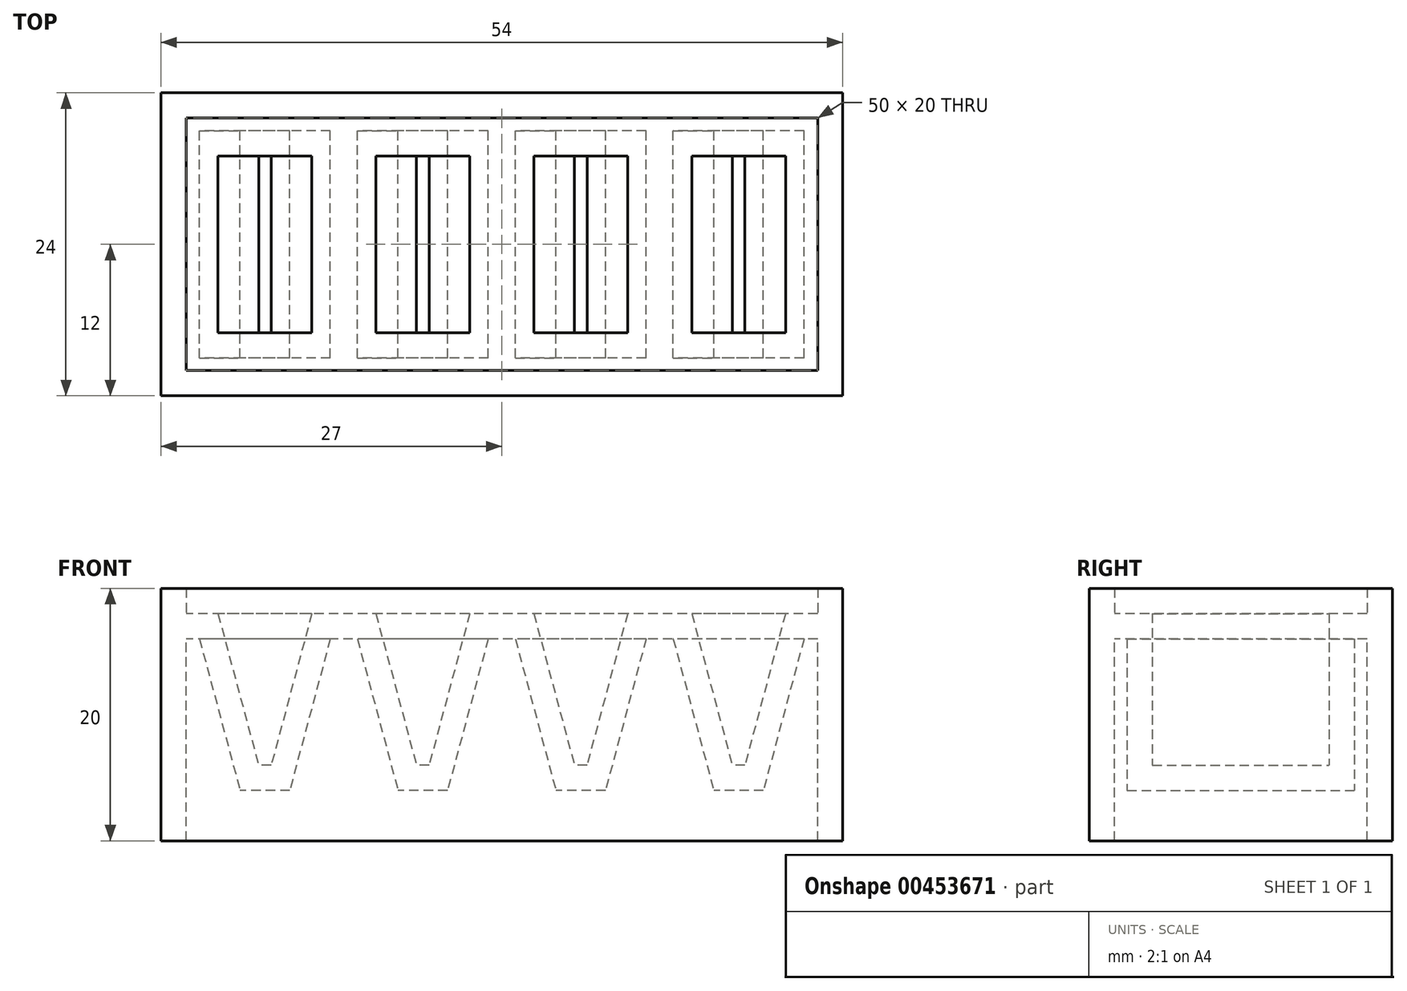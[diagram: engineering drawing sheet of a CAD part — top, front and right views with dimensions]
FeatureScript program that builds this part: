
annotation { "Feature Type Name" : "Feature", "Feature Type Description" : "" }
export const myFeature = defineFeature(function(context is Context, id is Id, definition is map)
    precondition{}
    {
        {
            var Q0;
            Q0=qCreatedBy(makeId("Right.planeOp"),FACE);
            var sketch = newSketch(context, id + "F0", { "sketchPlane" : qUnion([Q0])});
            skLineSegment(sketch, "E0", {"start": v(0, 0) * mm, "end": v(0, 18) * mm, "construction": true});
            skLineSegment(sketch, "E1", {"start": v(7, 18) * mm, "end": v(10, 18) * mm});
            skLineSegment(sketch, "E2", {"start": v(0, 0) * mm, "end": v(10, 0) * mm, "construction": true});
            skLineSegment(sketch, "E3", {"start": v(12, 0) * mm, "end": v(10, 0) * mm});
            skLineSegment(sketch, "E4", {"start": v(10, 0) * mm, "end": v(10, 16) * mm});
            skLineSegment(sketch, "E5", {"start": v(10, 16) * mm, "end": v(9, 16) * mm});
            skLineSegment(sketch, "E6", {"start": v(9, 16) * mm, "end": v(9, 4) * mm});
            skLineSegment(sketch, "E7", {"start": v(0, 4) * mm, "end": v(9, 4) * mm});
            skLineSegment(sketch, "E8", {"start": v(0, 6) * mm, "end": v(7, 6) * mm});
            skLineSegment(sketch, "E9", {"start": v(7, 18) * mm, "end": v(7, 6) * mm});
            skLineSegment(sketch, "E10.MirrorCS", {"start": v(0, 6) * mm, "end": v(-7, 6) * mm});
            skLineSegment(sketch, "E11.MirrorCS", {"start": v(0, 0) * mm, "end": v(-10, 0) * mm, "construction": true});
            skLineSegment(sketch, "E12.MirrorCS", {"start": v(0, 4) * mm, "end": v(-9, 4) * mm});
            skLineSegment(sketch, "E13.MirrorCS", {"start": v(-7, 18) * mm, "end": v(-7, 6) * mm});
            skLineSegment(sketch, "E14.MirrorCS", {"start": v(-12, 0) * mm, "end": v(-10, 0) * mm});
            skLineSegment(sketch, "E15.MirrorCS", {"start": v(-10, 0) * mm, "end": v(-10, 16) * mm});
            skLineSegment(sketch, "E16.MirrorCS", {"start": v(-10, 16) * mm, "end": v(-9, 16) * mm});
            skLineSegment(sketch, "E17.MirrorCS", {"start": v(-9, 16) * mm, "end": v(-9, 4) * mm});
            skLineSegment(sketch, "E18.bottom", {"start": v(10, 20) * mm, "end": v(12, 20) * mm});
            skLineSegment(sketch, "E18.left", {"start": v(10, 20) * mm, "end": v(10, 18) * mm});
            skLineSegment(sketch, "E19", {"start": v(10, 18) * mm, "end": v(10, 16) * mm, "construction": true});
            skLineSegment(sketch, "E20", {"start": v(12, 0) * mm, "end": v(12, 20) * mm});
            skLineSegment(sketch, "E21.MirrorCS", {"start": v(-7, 18) * mm, "end": v(-10, 18) * mm});
            skLineSegment(sketch, "E22.MirrorCS", {"start": v(-10, 20) * mm, "end": v(-10, 18) * mm});
            skLineSegment(sketch, "E23.MirrorCS", {"start": v(-10, 20) * mm, "end": v(-12, 20) * mm});
            skLineSegment(sketch, "E24.MirrorCS", {"start": v(-12, 0) * mm, "end": v(-12, 20) * mm});
            skSolve(sketch);
        }
        {
            var Q0;
            Q0=makeQuery(id+"F0.imprint","IMPRINT",FACE,{"disambiguationData":[TD([[makeQuery(id+"F0.imprint","IMPRINT",EDGE,{"derivedFrom":sQuery(id+"F0.wireOp",EDGE,"E1")}),-1.0]])]});
            extrude(context, id + "F1", {"entities" : qUnion([Q0]), "depth" : 50 * mm});
        }
        {
            var Q0;
            Q0=qCreatedBy(makeId("Front.planeOp"),FACE);
            var sketch = newSketch(context, id + "F2", { "sketchPlane" : qUnion([Q0])});
            skLineSegment(sketch, "E25.bottom", {"start": v(37.5, 20) * mm, "end": v(39.5, 20) * mm, "construction": true});
            skLineSegment(sketch, "E26", {"start": v(38.57, 16) * mm, "end": v(41.78, 4) * mm});
            skLineSegment(sketch, "E27", {"start": v(41.78, 4) * mm, "end": v(45.71, 4) * mm});
            skLineSegment(sketch, "E28", {"start": v(48.93, 16) * mm, "end": v(45.71, 4) * mm});
            skLineSegment(sketch, "E29", {"start": v(40.03, 18) * mm, "end": v(43.25, 6) * mm});
            skLineSegment(sketch, "E30", {"start": v(50, 20) * mm, "end": v(48, 20) * mm, "construction": true});
            skLineSegment(sketch, "E31", {"start": v(47.46, 18) * mm, "end": v(44.25, 6) * mm});
            skLineSegment(sketch, "E32", {"start": v(44.25, 6) * mm, "end": v(43.25, 6) * mm});
            skLineSegment(sketch, "E33", {"start": v(38.03, 18) * mm, "end": v(40.03, 18) * mm});
            skLineSegment(sketch, "E34", {"start": v(39.5, 20) * mm, "end": v(40.03, 18) * mm, "construction": true});
            skLineSegment(sketch, "E35", {"start": v(38.03, 18) * mm, "end": v(37.5, 20) * mm, "construction": true});
            skLineSegment(sketch, "E36", {"start": v(47.46, 18) * mm, "end": v(49.46, 18) * mm});
            skLineSegment(sketch, "E37", {"start": v(48, 20) * mm, "end": v(47.46, 18) * mm, "construction": true});
            skLineSegment(sketch, "E38", {"start": v(50, 20) * mm, "end": v(49.46, 18) * mm, "construction": true});
            skLineSegment(sketch, "E39", {"start": v(50, 16) * mm, "end": v(50, 4) * mm});
            skLineSegment(sketch, "E40", {"start": v(50, 4) * mm, "end": v(45.71, 4) * mm});
            skLineSegment(sketch, "E41", {"start": v(50, 16) * mm, "end": v(48.93, 16) * mm});
            skLineSegment(sketch, "E42", {"start": v(50, 16) * mm, "end": v(50, 20) * mm, "construction": true});
            skLineSegment(sketch, "E43", {"start": v(49.46, 18) * mm, "end": v(50, 18) * mm});
            skLineSegment(sketch, "E44", {"start": v(50, 16) * mm, "end": v(50, 18) * mm});
            skLineSegment(sketch, "E45", {"start": v(48.93, 16) * mm, "end": v(49.46, 18) * mm, "construction": true});
            skLineSegment(sketch, "E46", {"start": v(37.5, 20) * mm, "end": v(37.5, 18) * mm, "construction": true});
            skLineSegment(sketch, "E47", {"start": v(38.57, 16) * mm, "end": v(37.5, 16) * mm});
            skLineSegment(sketch, "E48", {"start": v(38.03, 18) * mm, "end": v(37.5, 18) * mm});
            skLineSegment(sketch, "E49", {"start": v(38.57, 16) * mm, "end": v(38.03, 18) * mm, "construction": true});
            skLineSegment(sketch, "E50", {"start": v(37.5, 4) * mm, "end": v(41.78, 4) * mm});
            skLineSegment(sketch, "E51.MirrorCS", {"start": v(36.43, 16) * mm, "end": v(37.5, 16) * mm});
            skLineSegment(sketch, "E52.MirrorCS", {"start": v(36.43, 16) * mm, "end": v(33.21, 4) * mm});
            skLineSegment(sketch, "E53.MirrorCS", {"start": v(33.21, 4) * mm, "end": v(29.28, 4) * mm});
            skLineSegment(sketch, "E54.MirrorCS", {"start": v(26.07, 16) * mm, "end": v(29.28, 4) * mm});
            skLineSegment(sketch, "E55.MirrorCS", {"start": v(25, 16) * mm, "end": v(26.07, 16) * mm});
            skLineSegment(sketch, "E56.MirrorCS", {"start": v(36.96, 18) * mm, "end": v(34.96, 18) * mm});
            skLineSegment(sketch, "E57.MirrorCS", {"start": v(36.96, 18) * mm, "end": v(37.5, 18) * mm});
            skLineSegment(sketch, "E58.MirrorCS", {"start": v(34.96, 18) * mm, "end": v(31.75, 6) * mm});
            skLineSegment(sketch, "E59.MirrorCS", {"start": v(30.75, 6) * mm, "end": v(31.75, 6) * mm});
            skLineSegment(sketch, "E60.MirrorCS", {"start": v(27.53, 18) * mm, "end": v(30.75, 6) * mm});
            skLineSegment(sketch, "E61.MirrorCS", {"start": v(27.53, 18) * mm, "end": v(25.53, 18) * mm});
            skLineSegment(sketch, "E62.MirrorCS", {"start": v(25.53, 18) * mm, "end": v(25, 18) * mm});
            skLineSegment(sketch, "E63.MirrorCS", {"start": v(25, 16) * mm, "end": v(25, 18) * mm, "construction": true});
            skLineSegment(sketch, "E64.MirrorCS", {"start": v(25, 4) * mm, "end": v(29.28, 4) * mm});
            skLineSegment(sketch, "E65.MirrorCS", {"start": v(37.5, 4) * mm, "end": v(33.21, 4) * mm});
            skLineSegment(sketch, "E66.MirrorCS", {"start": v(24.46, 18) * mm, "end": v(25, 18) * mm});
            skLineSegment(sketch, "E67.MirrorCS", {"start": v(22.46, 18) * mm, "end": v(24.46, 18) * mm});
            skLineSegment(sketch, "E68.MirrorCS", {"start": v(22.46, 18) * mm, "end": v(19.24, 6) * mm});
            skLineSegment(sketch, "E69.MirrorCS", {"start": v(19.24, 6) * mm, "end": v(18.24, 6) * mm});
            skLineSegment(sketch, "E70.MirrorCS", {"start": v(15.03, 18) * mm, "end": v(18.24, 6) * mm});
            skLineSegment(sketch, "E71.MirrorCS", {"start": v(13.03, 18) * mm, "end": v(15.03, 18) * mm});
            skLineSegment(sketch, "E72.MirrorCS", {"start": v(13.03, 18) * mm, "end": v(12.5, 18) * mm});
            skLineSegment(sketch, "E73.MirrorCS", {"start": v(11.96, 18) * mm, "end": v(12.5, 18) * mm});
            skLineSegment(sketch, "E74.MirrorCS", {"start": v(11.96, 18) * mm, "end": v(9.96, 18) * mm});
            skLineSegment(sketch, "E75.MirrorCS", {"start": v(9.96, 18) * mm, "end": v(6.74, 6) * mm});
            skLineSegment(sketch, "E76.MirrorCS", {"start": v(5.74, 6) * mm, "end": v(6.74, 6) * mm});
            skLineSegment(sketch, "E77.MirrorCS", {"start": v(2.53, 18) * mm, "end": v(5.74, 6) * mm});
            skLineSegment(sketch, "E78.MirrorCS", {"start": v(2.53, 18) * mm, "end": v(0.53, 18) * mm});
            skLineSegment(sketch, "E79.MirrorCS", {"start": v(0.53, 18) * mm, "end": v(-0.01, 18) * mm});
            skLineSegment(sketch, "E80.MirrorCS", {"start": v(-0.01, 16) * mm, "end": v(-0.01, 18) * mm});
            skLineSegment(sketch, "E81.MirrorCS", {"start": v(-0.01, 16) * mm, "end": v(1.06, 16) * mm});
            skLineSegment(sketch, "E82.MirrorCS", {"start": v(1.06, 16) * mm, "end": v(4.28, 4) * mm});
            skLineSegment(sketch, "E83.MirrorCS", {"start": v(8.2, 4) * mm, "end": v(4.28, 4) * mm});
            skLineSegment(sketch, "E84.MirrorCS", {"start": v(11.42, 16) * mm, "end": v(8.2, 4) * mm});
            skLineSegment(sketch, "E85.MirrorCS", {"start": v(11.42, 16) * mm, "end": v(12.5, 16) * mm});
            skLineSegment(sketch, "E86.MirrorCS", {"start": v(13.56, 16) * mm, "end": v(12.5, 16) * mm});
            skLineSegment(sketch, "E87.MirrorCS", {"start": v(13.56, 16) * mm, "end": v(16.78, 4) * mm});
            skLineSegment(sketch, "E88.MirrorCS", {"start": v(16.78, 4) * mm, "end": v(20.7, 4) * mm});
            skLineSegment(sketch, "E89.MirrorCS", {"start": v(23.92, 16) * mm, "end": v(20.7, 4) * mm});
            skLineSegment(sketch, "E90.MirrorCS", {"start": v(25, 16) * mm, "end": v(23.92, 16) * mm});
            skLineSegment(sketch, "E91.MirrorCS", {"start": v(25, 4) * mm, "end": v(20.7, 4) * mm});
            skPoint(sketch, "E92.MirrorCS.end.orphan", {"position": v(25, 4) * mm});
            skPoint(sketch, "E92.MirrorCS.start.orphan", {"position": v(25, 16) * mm});
            skLineSegment(sketch, "E93.MirrorCS", {"start": v(12.5, 4) * mm, "end": v(16.78, 4) * mm});
            skLineSegment(sketch, "E94.MirrorCS", {"start": v(12.5, 4) * mm, "end": v(8.2, 4) * mm});
            skLineSegment(sketch, "E95.MirrorCS", {"start": v(-0.01, 4) * mm, "end": v(4.28, 4) * mm});
            skLineSegment(sketch, "E96.MirrorCS", {"start": v(-0.01, 16) * mm, "end": v(-0.01, 4) * mm});
            skSolve(sketch);
        }
        {
            var Q0;
            Q0=makeQuery(id+"F2.imprint","IMPRINT",FACE,{"disambiguationData":[TD([[makeQuery(id+"F2.imprint","IMPRINT",EDGE,{"derivedFrom":sQuery(id+"F2.wireOp",EDGE,"E26")}),1.0]])]});
            var Q1;
            Q1=makeQuery(id+"F2.imprint","IMPRINT",FACE,{"disambiguationData":[TD([[makeQuery(id+"F2.imprint","IMPRINT",EDGE,{"derivedFrom":sQuery(id+"F2.wireOp",EDGE,"Oqk51IUW-a7Uu-kslN-KpYw-qfUBox6aqXp0")}),-1.0]])]});
            extrude(context, id + "F3", {"entities" : qUnion([Q0, Q1]), "operationType" : NewBodyOperationType.ADD, "endBound" : BoundingType.SYMMETRIC, "depth" : 18 * mm});
        }
        {
            var Q0;
            Q0=makeQuery(id+"F2.imprint","IMPRINT",FACE,{"disambiguationData":[TD([[makeQuery(id+"F2.imprint","IMPRINT",EDGE,{"derivedFrom":sQuery(id+"F2.wireOp",EDGE,"E39")}),-1.0]])]});
            var Q1;
            Q1=makeQuery(id+"F2.imprint","IMPRINT",FACE,{"disambiguationData":[TD([[makeQuery(id+"F2.imprint","IMPRINT",EDGE,{"derivedFrom":sQuery(id+"F2.wireOp",EDGE,"E26")}),-1.0]])]});
            var Q2;
            Q2=makeQuery(id+"F2.imprint","IMPRINT",FACE,{"disambiguationData":[TD([[makeQuery(id+"F2.imprint","IMPRINT",EDGE,{"derivedFrom":sQuery(id+"F2.wireOp",EDGE,"E54.MirrorCS")}),-1.0]])]});
            var Q3;
            Q3=makeQuery(id+"F2.imprint","IMPRINT",FACE,{"disambiguationData":[TD([[makeQuery(id+"F2.imprint","IMPRINT",EDGE,{"derivedFrom":sQuery(id+"F2.wireOp",EDGE,"E84.MirrorCS")}),1.0]])]});
            var Q4;
            Q4=makeQuery(id+"F2.imprint","IMPRINT",FACE,{"disambiguationData":[TD([[makeQuery(id+"F2.imprint","IMPRINT",EDGE,{"derivedFrom":sQuery(id+"F2.wireOp",EDGE,"E81.MirrorCS")}),-1.0]])]});
            extrude(context, id + "F4", {"entities" : qUnion([Q0, Q1, Q2, Q3, Q4]), "operationType" : NewBodyOperationType.REMOVE, "endBound" : BoundingType.SYMMETRIC, "depth" : 18 * mm});
        }
        {
            var Q0;
            Q0=makeQuery(id+"F3.boolean.opBoolean","MERGE",FACE,{"derivedFrom":[makeQuery(id+"F1.opExtrude","CAP_FACE",FACE,{"disambiguationData":[OSD([sQuery(id+"F0.wireOp",EDGE,"E1"),sQuery(id+"F0.wireOp",EDGE,"E3"),sQuery(id+"F0.wireOp",EDGE,"E4"),sQuery(id+"F0.wireOp",EDGE,"E5"),sQuery(id+"F0.wireOp",EDGE,"E6"),sQuery(id+"F0.wireOp",EDGE,"E7"),sQuery(id+"F0.wireOp",EDGE,"E8"),sQuery(id+"F0.wireOp",EDGE,"E9"),sQuery(id+"F0.wireOp",EDGE,"E10.MirrorCS"),sQuery(id+"F0.wireOp",EDGE,"E12.MirrorCS"),sQuery(id+"F0.wireOp",EDGE,"E13.MirrorCS"),sQuery(id+"F0.wireOp",EDGE,"E14.MirrorCS"),sQuery(id+"F0.wireOp",EDGE,"E15.MirrorCS"),sQuery(id+"F0.wireOp",EDGE,"E16.MirrorCS"),sQuery(id+"F0.wireOp",EDGE,"E17.MirrorCS"),sQuery(id+"F0.wireOp",EDGE,"E18.bottom"),sQuery(id+"F0.wireOp",EDGE,"E18.left"),sQuery(id+"F0.wireOp",EDGE,"E20"),sQuery(id+"F0.wireOp",EDGE,"E21.MirrorCS"),sQuery(id+"F0.wireOp",EDGE,"E22.MirrorCS"),sQuery(id+"F0.wireOp",EDGE,"E23.MirrorCS"),sQuery(id+"F0.wireOp",EDGE,"E24.MirrorCS")])],"isStart":false}),makeQuery(id+"F3.opExtrude","SWEPT_FACE",FACE,{"disambiguationData":[OSD([sQuery(id+"F2.wireOp",EDGE,"E44")])]})]});
            var sketch = newSketch(context, id + "F5", { "sketchPlane" : qUnion([Q0])});
            skLineSegment(sketch, "E97.bottom", {"start": v(-12, 20) * mm, "end": v(12, 20) * mm});
            skLineSegment(sketch, "E97.top", {"start": v(-12, 0) * mm, "end": v(12, 0) * mm});
            skLineSegment(sketch, "E97.left", {"start": v(-12, 20) * mm, "end": v(-12, 0) * mm});
            skLineSegment(sketch, "E97.right", {"start": v(12, 20) * mm, "end": v(12, 0) * mm});
            skSolve(sketch);
        }
        {
            var Q0;
            {var subQ1=makeQuery(id+"F1.opExtrude","CAP_EDGE",EDGE,{"disambiguationData":[OSD([sQuery(id+"F0.wireOp",EDGE,"E18.left")])],"isStart":false});Q0=makeQuery(id+"F5.imprint","IMPRINT",FACE,{"disambiguationData":[TD([[makeQuery(id+"F5.imprint","IMPRINT",EDGE,{"derivedFrom":subQ1}),-1.0]])]});}
            var Q1;
            {var subQ5=sQuery(id+"F5.wireOp",EDGE,"E97.left");Q1=makeQuery(id+"F5.imprint","IMPRINT",FACE,{"disambiguationData":[TD([[makeQuery(id+"F5.imprint","IMPRINT",EDGE,{"derivedFrom":subQ5}),-1.0]])]});}
            var Q2;
            {var subQ1=makeQuery(id+"F1.opExtrude","CAP_EDGE",EDGE,{"disambiguationData":[OSD([sQuery(id+"F0.wireOp",EDGE,"E4")])],"isStart":false});Q2=makeQuery(id+"F5.imprint","IMPRINT",FACE,{"disambiguationData":[TD([[makeQuery(id+"F5.imprint","IMPRINT",EDGE,{"derivedFrom":subQ1}),1.0]])]});}
            extrude(context, id + "F6", {"entities" : qUnion([Q0, Q1, Q2]), "operationType" : NewBodyOperationType.ADD, "depth" : 2 * mm});
        }
        {
            var Q0;
            {var subQ0=sQuery(id+"F0.wireOp",EDGE,"E24.MirrorCS");var subQ1=sQuery(id+"F0.wireOp",EDGE,"E23.MirrorCS");var subQ2=sQuery(id+"F0.wireOp",EDGE,"E22.MirrorCS");var subQ3=sQuery(id+"F0.wireOp",EDGE,"E21.MirrorCS");var subQ4=sQuery(id+"F0.wireOp",EDGE,"E17.MirrorCS");var subQ5=sQuery(id+"F0.wireOp",EDGE,"E16.MirrorCS");var subQ6=sQuery(id+"F0.wireOp",EDGE,"E1");var subQ7=sQuery(id+"F0.wireOp",EDGE,"E14.MirrorCS");var subQ13=sQuery(id+"F0.wireOp",EDGE,"E15.MirrorCS");var subQ14=makeQuery(id+"F1.opExtrude","CAP_FACE",FACE,{"disambiguationData":[OSD([subQ6,sQuery(id+"F0.wireOp",EDGE,"E3"),sQuery(id+"F0.wireOp",EDGE,"E4"),sQuery(id+"F0.wireOp",EDGE,"E5"),sQuery(id+"F0.wireOp",EDGE,"E6"),sQuery(id+"F0.wireOp",EDGE,"E7"),sQuery(id+"F0.wireOp",EDGE,"E8"),sQuery(id+"F0.wireOp",EDGE,"E9"),sQuery(id+"F0.wireOp",EDGE,"E10.MirrorCS"),sQuery(id+"F0.wireOp",EDGE,"E12.MirrorCS"),sQuery(id+"F0.wireOp",EDGE,"E13.MirrorCS"),subQ7,subQ13,subQ5,subQ4,sQuery(id+"F0.wireOp",EDGE,"E18.bottom"),sQuery(id+"F0.wireOp",EDGE,"E18.left"),sQuery(id+"F0.wireOp",EDGE,"E20"),subQ3,subQ2,subQ1,subQ0])],"isStart":true});Q0=makeQuery(id+"F3.boolean.opBoolean","SPLIT",FACE,{"disambiguationData":[TD([makeQuery(id+"F1.opExtrude","SWEPT_FACE",FACE,{"disambiguationData":[OSD([subQ7])]})])],"derivedFrom":subQ14});}
            var sketch = newSketch(context, id + "F7", { "sketchPlane" : qUnion([Q0])});
            skLineSegment(sketch, "E98.bottom", {"start": v(-12, 20) * mm, "end": v(12, 20) * mm});
            skLineSegment(sketch, "E98.top", {"start": v(-12, 0) * mm, "end": v(12, 0) * mm});
            skLineSegment(sketch, "E98.left", {"start": v(-12, 20) * mm, "end": v(-12, 0) * mm});
            skLineSegment(sketch, "E98.right", {"start": v(12, 20) * mm, "end": v(12, 0) * mm});
            skSolve(sketch);
        }
        {
            var Q0;
            {var subQ0=sQuery(id+"F7.wireOp",EDGE,"E98.right");Q0=makeQuery(id+"F7.imprint","IMPRINT",FACE,{"disambiguationData":[TD([[makeQuery(id+"F7.imprint","IMPRINT",EDGE,{"derivedFrom":subQ0}),1.0]])]});}
            var Q1;
            {var subQ2=sQuery(id+"F7.wireOp",EDGE,"E98.left");Q1=makeQuery(id+"F7.imprint","IMPRINT",FACE,{"disambiguationData":[TD([[makeQuery(id+"F7.imprint","IMPRINT",EDGE,{"derivedFrom":subQ2}),1.0]])]});}
            extrude(context, id + "F8", {"entities" : qUnion([Q0, Q1]), "operationType" : NewBodyOperationType.ADD, "depth" : 2 * mm});
        }
    });
